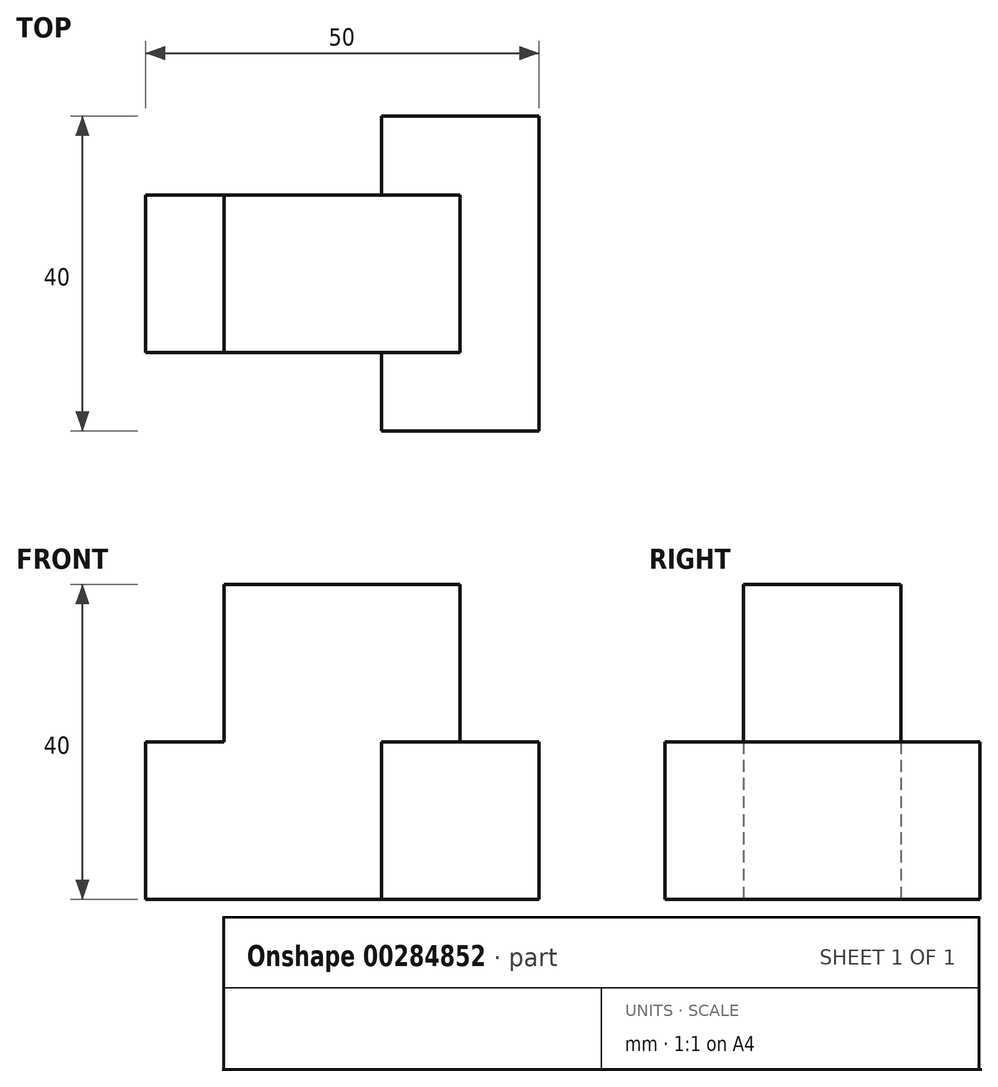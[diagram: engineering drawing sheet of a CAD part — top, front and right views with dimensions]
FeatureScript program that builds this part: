
annotation { "Feature Type Name" : "Feature", "Feature Type Description" : "" }
export const myFeature = defineFeature(function(context is Context, id is Id, definition is map)
    precondition{}
    {
        {
            var Q0;
            Q0=qCreatedBy(makeId("Front.planeOp"),FACE);
            var sketch = newSketch(context, id + "F0", { "sketchPlane" : qUnion([Q0])});
            skLineSegment(sketch, "E0.bottom", {"start": v(0, 0) * mm, "end": v(50, 0) * mm});
            skLineSegment(sketch, "E0.top", {"start": v(0, 40) * mm, "end": v(50, 40) * mm});
            skLineSegment(sketch, "E0.left", {"start": v(0, 0) * mm, "end": v(0, 40) * mm});
            skLineSegment(sketch, "E0.right", {"start": v(50, 0) * mm, "end": v(50, 40) * mm});
            skSolve(sketch);
        }
        {
            var Q0;
            Q0=makeQuery(id+"F0.imprint","IMPRINT",FACE,{"disambiguationData":[TD([[makeQuery(id+"F0.imprint","IMPRINT",EDGE,{"derivedFrom":sQuery(id+"F0.wireOp",EDGE,"E0.bottom")}),1.0]])]});
            extrude(context, id + "F1", {"entities" : qUnion([Q0]), "depth" : 40 * mm});
        }
        {
            var Q0;
            Q0=makeQuery(id+"F1.opExtrude","SWEPT_FACE",FACE,{"disambiguationData":[OSD([sQuery(id+"F0.wireOp",EDGE,"E0.left")])]});
            var sketch = newSketch(context, id + "F2", { "sketchPlane" : qUnion([Q0])});
            skLineSegment(sketch, "E1", {"start": v(0, 20) * mm, "end": v(40, 20) * mm});
            skLineSegment(sketch, "E2", {"start": v(30, 40) * mm, "end": v(30, 20) * mm});
            skLineSegment(sketch, "E3", {"start": v(10, 40) * mm, "end": v(10, 20) * mm});
            skLineSegment(sketch, "E4.0", {"start": v(40, 40) * mm, "end": v(0, 40) * mm});
            skLineSegment(sketch, "E5.0.1", {"start": v(40, 40) * mm, "end": v(40, 20) * mm});
            skLineSegment(sketch, "E5.0.3", {"start": v(40, 20) * mm, "end": v(40, 40) * mm});
            skLineSegment(sketch, "E6.0.1", {"start": v(0, 40) * mm, "end": v(0, 20) * mm});
            skLineSegment(sketch, "E6.0.3", {"start": v(0, 0) * mm, "end": v(0, 40) * mm});
            skPoint(sketch, "E7.orphan", {"position": v(40, 0) * mm});
            skPoint(sketch, "E8.orphan", {"position": v(0, 0) * mm});
            skSolve(sketch);
        }
        {
            var Q0;
            {var subQ3=sQuery(id+"F2.wireOp",EDGE,"E3");Q0=makeQuery(id+"F2.imprint","IMPRINT",FACE,{"disambiguationData":[TD([[makeQuery(id+"F2.imprint","IMPRINT",EDGE,{"derivedFrom":subQ3}),-1.0]])]});}
            var Q1;
            {var subQ2=sQuery(id+"F2.wireOp",EDGE,"E2");Q1=makeQuery(id+"F2.imprint","IMPRINT",FACE,{"disambiguationData":[TD([[makeQuery(id+"F2.imprint","IMPRINT",EDGE,{"derivedFrom":subQ2}),1.0]])]});}
            extrude(context, id + "F3", {"entities" : qUnion([Q0, Q1]), "operationType" : NewBodyOperationType.REMOVE, "endBound" : BoundingType.THROUGH_ALL, "oppositeDirection" : true, "depth" : 30 * mm});
        }
        {
            var Q0;
            {var subQ0=sQuery(id+"F2.wireOp",EDGE,"E1");Q0=makeQuery(id+"F3.boolean.opBoolean","COPY",FACE,{"derivedFrom":makeQuery(id+"F3.opExtrude","SWEPT_FACE",FACE,{"disambiguationData":[OSD([subQ0]),TDD([makeQuery(id+"F2.imprint","IMPRINT",EDGE,{"disambiguationData":[TD([[makeQuery(id+"F2.imprint","INTERSECT",VERTEX,{"derivedFrom":[subQ0,sQuery(id+"F2.wireOp",EDGE,"E6.0.3")]}),-1.0]])],"derivedFrom":subQ0})])]})});}
            var sketch = newSketch(context, id + "F4", { "sketchPlane" : qUnion([Q0])});
            skLineSegment(sketch, "E9.0", {"start": v(50, 0) * mm, "end": v(30, 0) * mm});
            skLineSegment(sketch, "E10.0", {"start": v(50, -10) * mm, "end": v(30, -10) * mm});
            skLineSegment(sketch, "E11.0", {"start": v(50, -30) * mm, "end": v(30, -30) * mm});
            skLineSegment(sketch, "E12.0", {"start": v(50, -40) * mm, "end": v(30, -40) * mm});
            skLineSegment(sketch, "E13", {"start": v(30, 0) * mm, "end": v(30, -10) * mm});
            skLineSegment(sketch, "E14", {"start": v(30, -30) * mm, "end": v(30, -40) * mm});
            skLineSegment(sketch, "E15.0", {"start": v(50, -30) * mm, "end": v(50, -40) * mm});
            skLineSegment(sketch, "E16.0", {"start": v(50, 0) * mm, "end": v(50, -10) * mm});
            skPoint(sketch, "E17.orphan", {"position": v(0, -10) * mm});
            skPoint(sketch, "E18.orphan", {"position": v(0, -30) * mm});
            skPoint(sketch, "E19.orphan", {"position": v(0, -40) * mm});
            skPoint(sketch, "E20.orphan", {"position": v(0, 0) * mm});
            skLineSegment(sketch, "E21.0", {"start": v(50, 0) * mm, "end": v(0, 0) * mm});
            skLineSegment(sketch, "E22.0", {"start": v(50, -10) * mm, "end": v(0, -10) * mm});
            skLineSegment(sketch, "E23.0", {"start": v(0, 0) * mm, "end": v(0, -10) * mm});
            skLineSegment(sketch, "E24.0", {"start": v(0, -30) * mm, "end": v(0, -40) * mm});
            skLineSegment(sketch, "E25.0", {"start": v(50, -40) * mm, "end": v(0, -40) * mm});
            skLineSegment(sketch, "E26.0", {"start": v(50, -30) * mm, "end": v(0, -30) * mm});
            skSolve(sketch);
        }
        {
            var Q0;
            {var subQ0=sQuery(id+"F4.wireOp",EDGE,"E13");Q0=makeQuery(id+"F4.imprint","IMPRINT",FACE,{"disambiguationData":[TD([[makeQuery(id+"F4.imprint","IMPRINT",EDGE,{"derivedFrom":subQ0}),-1.0]])]});}
            var Q1;
            {var subQ0=sQuery(id+"F4.wireOp",EDGE,"E14");Q1=makeQuery(id+"F4.imprint","IMPRINT",FACE,{"disambiguationData":[TD([[makeQuery(id+"F4.imprint","IMPRINT",EDGE,{"derivedFrom":subQ0}),-1.0]])]});}
            extrude(context, id + "F5", {"entities" : qUnion([Q0, Q1]), "operationType" : NewBodyOperationType.REMOVE, "endBound" : BoundingType.THROUGH_ALL, "oppositeDirection" : true, "depth" : 25 * mm});
        }
        {
            var Q0;
            Q0=makeQuery(id+"F1.opExtrude","SWEPT_FACE",FACE,{"disambiguationData":[OSD([sQuery(id+"F0.wireOp",EDGE,"E0.top")])]});
            var sketch = newSketch(context, id + "F6", { "sketchPlane" : qUnion([Q0])});
            skLineSegment(sketch, "E27", {"start": v(40, -10) * mm, "end": v(40, -30) * mm});
            skLineSegment(sketch, "E28.0", {"start": v(50, -10) * mm, "end": v(0, -10) * mm});
            skLineSegment(sketch, "E29.0", {"start": v(50, -30) * mm, "end": v(50, -10) * mm});
            skLineSegment(sketch, "E30.0", {"start": v(50, -30) * mm, "end": v(0, -30) * mm});
            skSolve(sketch);
        }
        {
            var Q0;
            Q0 = qSketchRegion(id + "F6", true);
            var Q1;
            {var subQ0=sQuery(id+"F2.wireOp",EDGE,"E1");Q1=makeQuery(id+"F3.boolean.opBoolean","COPY",FACE,{"derivedFrom":makeQuery(id+"F3.opExtrude","SWEPT_FACE",FACE,{"disambiguationData":[OSD([subQ0]),TDD([makeQuery(id+"F2.imprint","IMPRINT",EDGE,{"disambiguationData":[TD([[makeQuery(id+"F2.imprint","INTERSECT",VERTEX,{"derivedFrom":[subQ0,sQuery(id+"F2.wireOp",EDGE,"E6.0.3")]}),-1.0]])],"derivedFrom":subQ0})])]})});}
            extrude(context, id + "F7", {"entities" : qUnion([Q0]), "operationType" : NewBodyOperationType.REMOVE, "endBound" : BoundingType.UP_TO_SURFACE, "oppositeDirection" : true, "endBoundEntityFace" : qUnion([Q1]), "depth" : 25 * mm});
        }
        {
            var Q0;
            Q0=makeQuery(id+"F5.boolean.opBoolean","MERGE",FACE,{"derivedFrom":[makeQuery(id+"F3.boolean.opBoolean","COPY",FACE,{"derivedFrom":makeQuery(id+"F3.opExtrude","SWEPT_FACE",FACE,{"disambiguationData":[OSD([sQuery(id+"F2.wireOp",EDGE,"E2")])]})}),makeQuery(id+"F5.opExtrude","SWEPT_FACE",FACE,{"disambiguationData":[OSD([sQuery(id+"F4.wireOp",EDGE,"E26.0")])]})]});
            var sketch = newSketch(context, id + "F8", { "sketchPlane" : qUnion([Q0])});
            skLineSegment(sketch, "E31.bottom", {"start": v(0, 40) * mm, "end": v(10, 40) * mm});
            skLineSegment(sketch, "E31.top", {"start": v(0, 20) * mm, "end": v(10, 20) * mm});
            skLineSegment(sketch, "E31.left", {"start": v(0, 40) * mm, "end": v(0, 20) * mm});
            skLineSegment(sketch, "E31.right", {"start": v(10, 40) * mm, "end": v(10, 20) * mm});
            skSolve(sketch);
        }
        {
            var Q0;
            Q0 = qSketchRegion(id + "F8", true);
            extrude(context, id + "F9", {"entities" : qUnion([Q0]), "operationType" : NewBodyOperationType.REMOVE, "endBound" : BoundingType.THROUGH_ALL, "oppositeDirection" : true, "depth" : 25 * mm});
        }
    });
